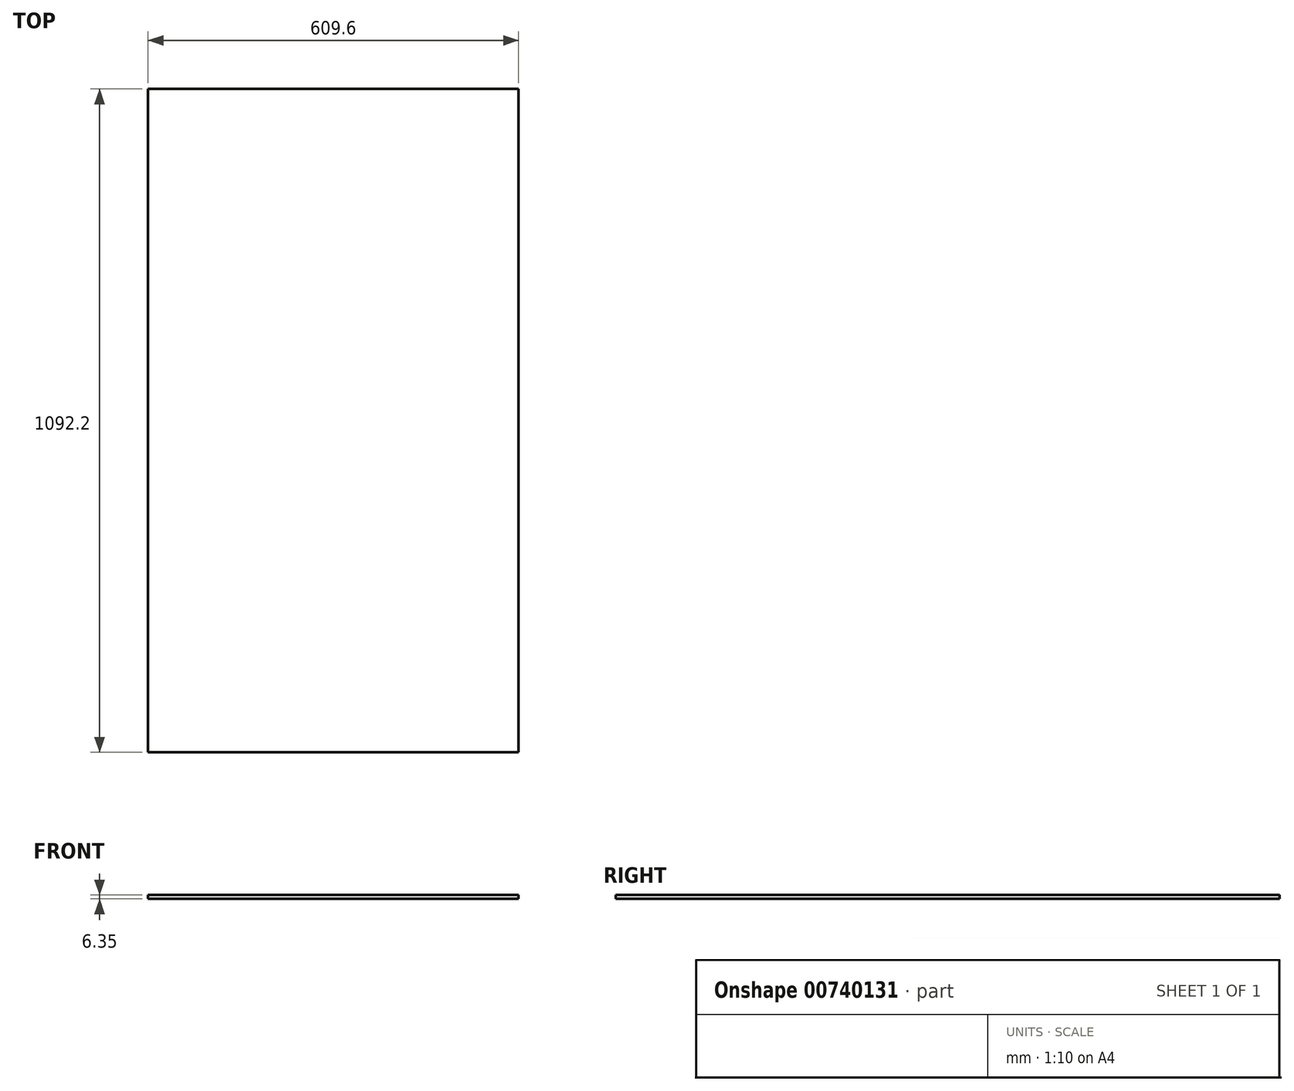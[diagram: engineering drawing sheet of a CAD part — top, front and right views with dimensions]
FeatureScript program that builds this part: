
annotation { "Feature Type Name" : "Feature", "Feature Type Description" : "" }
export const myFeature = defineFeature(function(context is Context, id is Id, definition is map)
    precondition{}
    {
        {
            var Q0;
            Q0=qCreatedBy(makeId("Top.planeOp"),FACE);
            var sketch = newSketch(context, id + "F0", { "sketchPlane" : qUnion([Q0])});
            skLineSegment(sketch, "E0.bottom", {"start": v(631.9, -203.66) * mm, "end": v(22.3, -203.66) * mm});
            skLineSegment(sketch, "E0.top", {"start": v(631.9, 888.54) * mm, "end": v(22.3, 888.54) * mm});
            skLineSegment(sketch, "E0.left", {"start": v(631.9, -203.66) * mm, "end": v(631.9, 888.54) * mm});
            skLineSegment(sketch, "E0.right", {"start": v(22.3, -203.66) * mm, "end": v(22.3, 888.54) * mm});
            skSolve(sketch);
        }
        {
            var Q0;
            Q0=makeQuery(id+"F0.imprint","IMPRINT",FACE,{"disambiguationData":[TD([[makeQuery(id+"F0.imprint","IMPRINT",EDGE,{"derivedFrom":sQuery(id+"F0.wireOp",EDGE,"E0.right")}),1.0]])]});
            var Q1;
            Q1=makeQuery(id+"F0.imprint","IMPRINT",FACE,{"disambiguationData":[TD([[makeQuery(id+"F0.imprint","IMPRINT",EDGE,{"derivedFrom":sQuery(id+"F0.wireOp",EDGE,"E0.bottom")}),-1.0]])]});
            extrude(context, id + "F1", {"entities" : qUnion([Q0, Q1]), "depth" : 6.35 * mm, "offsetDistance" : 25.4 * mm});
        }
    });
